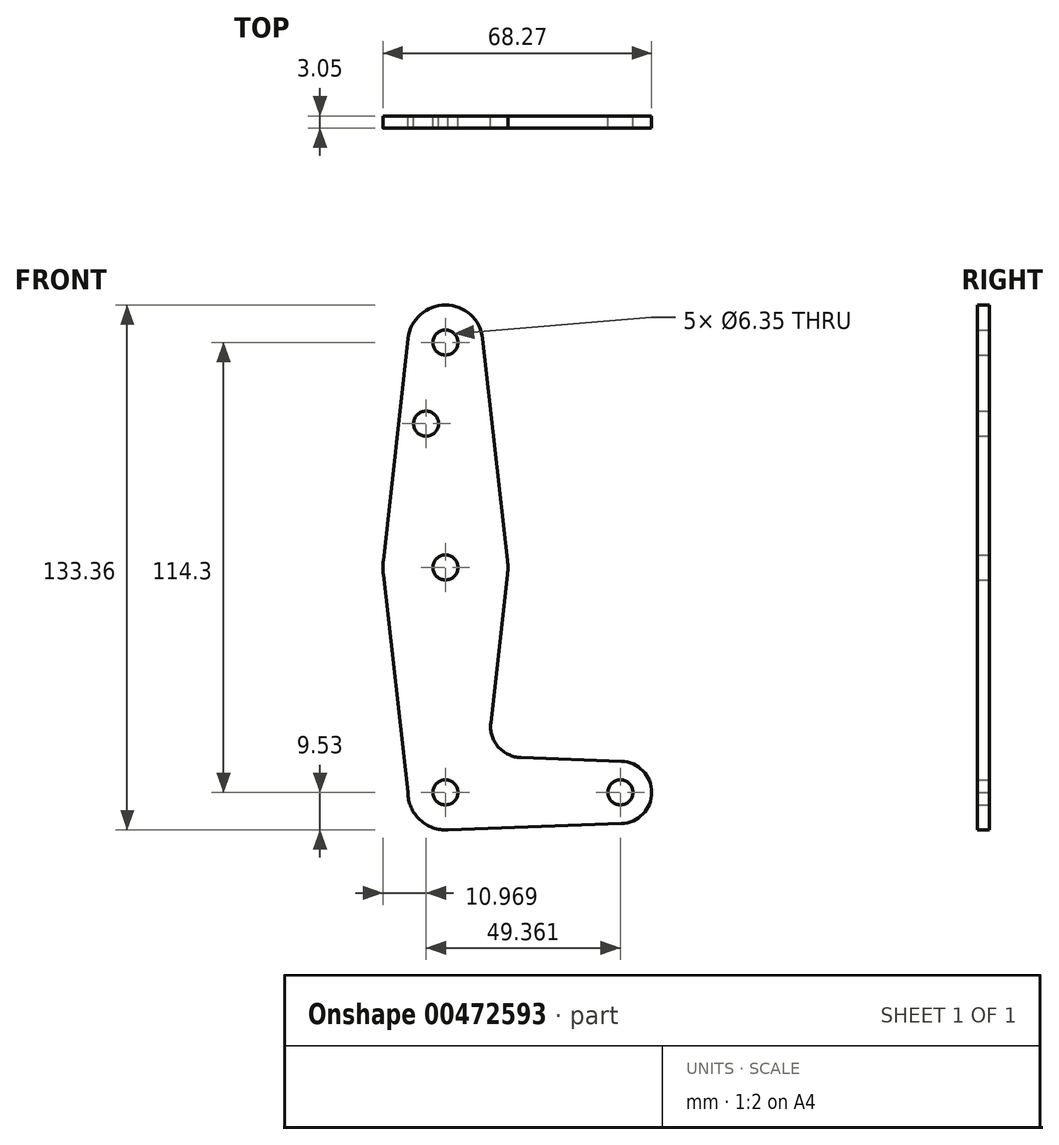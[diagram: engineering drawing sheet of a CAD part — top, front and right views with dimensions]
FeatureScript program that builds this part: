
annotation { "Feature Type Name" : "Feature", "Feature Type Description" : "" }
export const myFeature = defineFeature(function(context is Context, id is Id, definition is map)
    precondition{}
    {
        {
            var Q0;
            Q0=qCreatedBy(makeId("Front.planeOp"),FACE);
            var sketch = newSketch(context, id + "F0", { "sketchPlane" : qUnion([Q0])});
            skLineSegment(sketch, "E0", {"start": v(0, 114.3) * mm, "end": v(0, 0) * mm, "construction": true});
            skLineSegment(sketch, "E1", {"start": v(0, 0) * mm, "end": v(44.45, 0) * mm, "construction": true});
            skCircle(sketch, "E2", {"center": v(0, 114.3) * mm, "radius": 9.53 * mm});
            skCircle(sketch, "E3", {"center": v(0, 0) * mm, "radius": 9.53 * mm});
            skCircle(sketch, "E4", {"center": v(44.45, 0) * mm, "radius": 7.94 * mm});
            skCircle(sketch, "E5", {"center": v(0, 57.15) * mm, "radius": 15.88 * mm});
            skLineSegment(sketch, "E6", {"start": v(-9.47, 115.36) * mm, "end": v(-15.78, 58.91) * mm});
            skLineSegment(sketch, "E7", {"start": v(-9.52, 0) * mm, "end": v(-15.77, 55.37) * mm});
            skLineSegment(sketch, "E8", {"start": v(11.52, 17.68) * mm, "end": v(15.78, 55.39) * mm});
            skLineSegment(sketch, "E9", {"start": v(19.14, 8.84) * mm, "end": v(44.73, 7.93) * mm});
            skLineSegment(sketch, "E10", {"start": v(0, -9.53) * mm, "end": v(44.73, -7.93) * mm});
            skArc(sketch, "E11.filletArc", {"start": v(11.52, 17.68) * mm, "mid": v(13.4, 11.6) * mm, "end": v(19.14, 8.84) * mm});
            skCircle(sketch, "E12", {"center": v(0, 57.15) * mm, "radius": 3.18 * mm});
            skCircle(sketch, "E13", {"center": v(0, 114.3) * mm, "radius": 3.18 * mm});
            skCircle(sketch, "E14", {"center": v(0, 0) * mm, "radius": 3.18 * mm});
            skCircle(sketch, "E15", {"center": v(44.45, 0) * mm, "radius": 3.18 * mm});
            skCircle(sketch, "E16", {"center": v(-4.91, 93.68) * mm, "radius": 3.18 * mm});
            skLineSegment(sketch, "E17", {"start": v(9.47, 115.36) * mm, "end": v(15.78, 58.91) * mm});
            skSolve(sketch);
        }
        {
            var Q0;
            Q0 = qSketchRegion(id + "F0", true);
            extrude(context, id + "F1", {"entities" : qUnion([Q0]), "depth" : 3.05 * mm});
        }
    });
